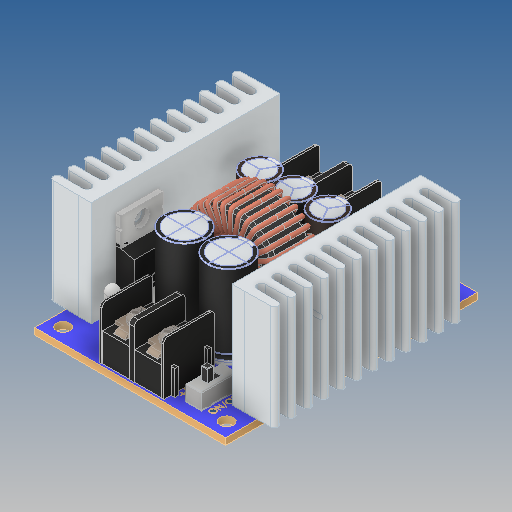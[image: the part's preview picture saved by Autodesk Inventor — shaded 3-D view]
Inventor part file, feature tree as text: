
AUTODESK INVENTOR PART (.ipt)
format: ipt  version: 2018 (Build 220112000, 112)  size: 7,849,472 bytes
history: native  units: mm
features: other x38, helix x37, surface_op x2
ambient origin geometry x8: Origin, YZ Plane, XZ Plane, XY Plane, X Axis, Y Axis, Z Axis, Center Point
bodies: Solid1 (feature_tree), Solid2 (feature_tree), Solid3 (feature_tree), Solid4 (feature_tree), Solid5 (feature_tree), Solid6 (feature_tree), Solid7 (feature_tree), Solid8 (feature_tree), Solid9 (feature_tree), Solid10 (feature_tree), Solid11 (feature_tree), Solid12 (feature_tree), Solid13 (feature_tree), Solid14 (feature_tree), Solid15 (feature_tree), Solid16 (feature_tree), Solid17 (feature_tree), Solid18 (feature_tree), Solid19 (feature_tree), Solid20 (feature_tree), Solid21 (feature_tree), Solid22 (feature_tree), Solid23 (feature_tree), Solid24 (feature_tree), Solid25 (feature_tree), Solid26 (feature_tree), Solid27 (feature_tree), Solid28 (feature_tree), Solid29 (feature_tree), Solid30 (feature_tree), Solid31 (feature_tree), Solid32 (feature_tree), Solid33 (feature_tree), Solid34 (feature_tree), Solid35 (feature_tree), Solid36 (feature_tree), Solid37 (feature_tree), Solid38 (feature_tree), Solid39 (feature_tree), Solid40 (feature_tree), Solid41 (feature_tree), Solid42 (feature_tree), Solid43 (feature_tree), Solid44 (feature_tree), Solid45 (feature_tree), Solid46 (feature_tree), Solid47 (feature_tree), Solid48 (feature_tree), Solid49 (feature_tree), Solid50 (feature_tree), Solid51 (feature_tree), Solid52 (feature_tree), Solid53 (feature_tree), Solid54 (feature_tree), Solid55 (feature_tree), Solid56 (feature_tree), Solid57 (feature_tree), Solid58 (feature_tree), Solid59 (feature_tree), Solid60 (feature_tree), Solid61 (feature_tree), Solid62 (feature_tree), Solid63 (feature_tree), Solid64 (feature_tree), Solid65 (feature_tree), Solid66 (feature_tree), Solid67 (feature_tree), Solid68 (feature_tree), Solid69 (feature_tree), Solid70 (feature_tree), Solid71 (feature_tree), Solid72 (feature_tree), Solid73 (feature_tree), Solid74 (feature_tree), Solid75 (feature_tree), Solid76 (feature_tree), Solid77 (feature_tree)
feature tree (77):
  other  "heatsink 45x10x12r_1:1"
  other  "pcb_2:1"
  other  "heatsink 45x10x12r_3:1"
  helix  "coil_4:1"  [1 undecoded]
  helix  "coil_4:2"  [1 undecoded]
  helix  "coil_4:3"  [1 undecoded]
  helix  "coil_4:4"  [1 undecoded]
  helix  "coil_4:5"  [1 undecoded]
  helix  "coil_4:6"  [1 undecoded]
  helix  "coil_4:7"  [1 undecoded]
  helix  "coil_4:8"  [1 undecoded]
  helix  "coil_4:9"  [1 undecoded]
  helix  "coil_4:10"  [1 undecoded]
  helix  "coil_4:11"  [1 undecoded]
  helix  "coil_4:12"  [1 undecoded]
  helix  "coil_4:13"  [1 undecoded]
  helix  "coil_4:14"  [1 undecoded]
  helix  "coil_4:15"  [1 undecoded]
  helix  "coil_4:16"  [1 undecoded]
  helix  "coil_4:17"  [1 undecoded]
  helix  "coil_4:18"  [1 undecoded]
  helix  "coil_4:19"  [1 undecoded]
  helix  "coil_4:20"  [1 undecoded]
  helix  "coil_4:21"  [1 undecoded]
  helix  "coil_4:22"  [1 undecoded]
  helix  "coil_4:23"  [1 undecoded]
  helix  "coil_4:24"  [1 undecoded]
  helix  "coil_4:25"  [1 undecoded]
  helix  "coil_4:26"  [1 undecoded]
  helix  "coil_4:27"  [1 undecoded]
  helix  "coil_4:28"  [1 undecoded]
  helix  "coil_4:29"  [1 undecoded]
  helix  "coil_4:30"  [1 undecoded]
  helix  "coil_4:31"  [1 undecoded]
  helix  "coil_4:32"  [1 undecoded]
  helix  "coil_4:33"  [1 undecoded]
  helix  "coil_4:34"  [1 undecoded]
  helix  "coil_4:35"  [1 undecoded]
  helix  "coil_4:36"  [1 undecoded]
  helix  "coil_4:37"  [1 undecoded]
  other  "terminal-Base_18:1"
  other  "screw pad_19:1"
  other  "screw-term_20:1"
  other  "screw pad_21:1"
  other  "screw-term_22:1"
  other  "terminal-Base_18:2"
  other  "screw pad_19:2"
  other  "screw-term_20:2"
  other  "screw pad_21:2"
  other  "screw-term_22:2"
  surface_op  "Trimpot 3296W_Valor predeterminado_7:1"
  surface_op  "Trimpot 3296W_Valor predeterminado_8:1"
  other  "c20x10x5_9:1"
  other  "c20x10x5_9:2"
  other  "c20x10x5_10:1"
  other  "c20x10x5_10:2"
  other  "c20x8x4_11:1"
  other  "c20x8x4_11:2"
  other  "c20x8x4_12:1"
  other  "c20x8x4_12:2"
  other  "c20x8x4_13:1"
  other  "c20x8x4_13:2"
  other  "MOSFET_14:1"
  other  "MOSFET_14:2"
  other  "MOSFET_14:3"
  other  "MOSFET_14:4"
  other  "MOSFET_14:5"
  other  "MOSFET_15:1"
  other  "MOSFET_15:2"
  other  "MOSFET_15:3"
  other  "MOSFET_15:4"
  other  "MOSFET_15:5"
  other  "3mm LED_16:1"
  other  "3mm LED_16:2"
  other  "3mm LED_16:3"
  other  "3mm LED_16:4"
  other  "Selector Switch - SS12D00_17:1"
note: 37 required parameter values undecoded (feature->parameter linkage not recoverable at this tier; creation-order binding heuristic only, values carry confidence <= 0.55)
